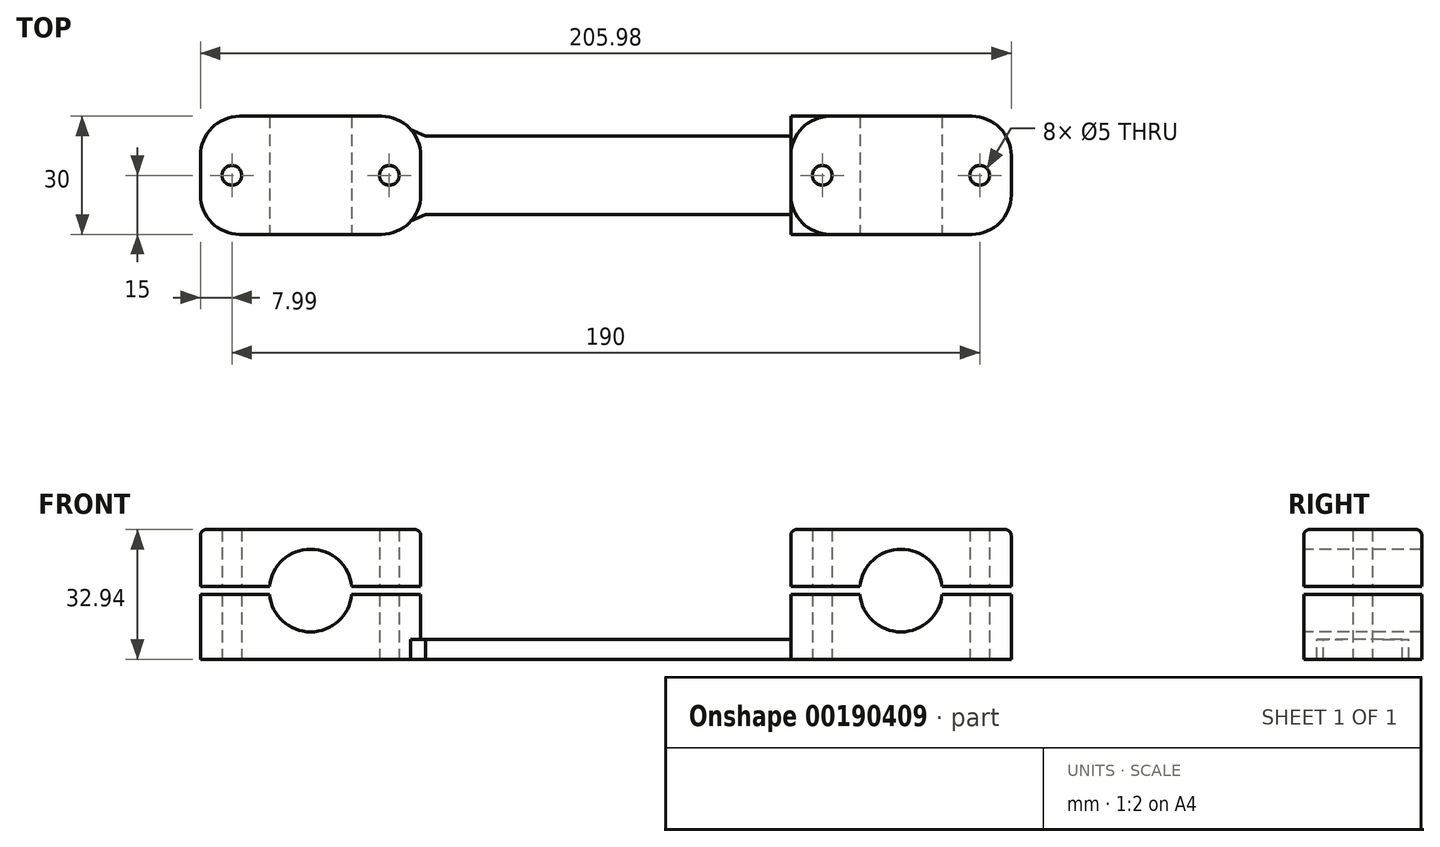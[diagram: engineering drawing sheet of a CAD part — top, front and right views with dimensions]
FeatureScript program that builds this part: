
annotation { "Feature Type Name" : "Feature", "Feature Type Description" : "" }
export const myFeature = defineFeature(function(context is Context, id is Id, definition is map)
    precondition{}
    {
        {
            var Q0;
            Q0=qCreatedBy(makeId("Top.planeOp"),FACE);
            var sketch = newSketch(context, id + "F0", { "sketchPlane" : qUnion([Q0])});
            skLineSegment(sketch, "E0.bottom", {"start": v(103, 15) * mm, "end": v(-103, 15) * mm});
            skLineSegment(sketch, "E0.top", {"start": v(103, -15) * mm, "end": v(-103, -15) * mm});
            skLineSegment(sketch, "E0.left", {"start": v(103, 15) * mm, "end": v(103, -15) * mm});
            skLineSegment(sketch, "E0.right", {"start": v(-103, 15) * mm, "end": v(-103, -15) * mm});
            skPoint(sketch, "E0.middle", {"position": v(0, 0) * mm});
            skLineSegment(sketch, "E1", {"start": v(75, 6.2) * mm, "end": v(75, -7.56) * mm, "construction": true});
            skCircle(sketch, "E2", {"center": v(95, 0) * mm, "radius": 2.5 * mm});
            skCircle(sketch, "E3.MirrorC", {"center": v(55, 0) * mm, "radius": 2.5 * mm});
            skCircle(sketch, "E4.MirrorC", {"center": v(-55, 0) * mm, "radius": 2.5 * mm});
            skCircle(sketch, "E5.MirrorC", {"center": v(-95, 0) * mm, "radius": 2.5 * mm});
            skLineSegment(sketch, "E6.MirrorCS", {"start": v(-75, 6.2) * mm, "end": v(-75, -7.56) * mm, "construction": true});
            skSolve(sketch);
        }
        {
            var Q0;
            Q0 = qSketchRegion(id + "F0", true);
            extrude(context, id + "F1", {"entities" : qUnion([Q0]), "depth" : 5 * mm});
        }
        {
            var Q0;
            Q0=makeQuery(id+"F1.opExtrude","SWEPT_FACE",FACE,{"disambiguationData":[OSD([sQuery(id+"F0.wireOp",EDGE,"E0.top")])]});
            var sketch = newSketch(context, id + "F2", { "sketchPlane" : qUnion([Q0])});
            skCircle(sketch, "E7", {"center": v(-75, 17.44) * mm, "radius": 10.5 * mm});
            skLineSegment(sketch, "E8.bottom", {"start": v(-103, 5) * mm, "end": v(-47, 5) * mm});
            skLineSegment(sketch, "E8.top", {"start": v(-103, 32.94) * mm, "end": v(-47, 32.94) * mm});
            skLineSegment(sketch, "E8.left", {"start": v(-103, 5) * mm, "end": v(-103, 32.94) * mm});
            skLineSegment(sketch, "E8.right", {"start": v(-47, 5) * mm, "end": v(-47, 32.94) * mm});
            skLineSegment(sketch, "E9", {"start": v(-75, 17.44) * mm, "end": v(-75, 36.32) * mm, "construction": true});
            skLineSegment(sketch, "E10.MirrorCS", {"start": v(75, 17.44) * mm, "end": v(75, 36.32) * mm, "construction": true});
            skLineSegment(sketch, "E11.MirrorCS", {"start": v(47, 5) * mm, "end": v(47, 32.94) * mm});
            skLineSegment(sketch, "E12.MirrorCS", {"start": v(103, 5) * mm, "end": v(103, 32.94) * mm});
            skLineSegment(sketch, "E13.MirrorCS", {"start": v(103, 32.94) * mm, "end": v(47, 32.94) * mm});
            skCircle(sketch, "E14.MirrorC", {"center": v(75, 17.44) * mm, "radius": 10.5 * mm});
            skLineSegment(sketch, "E15.MirrorCS", {"start": v(103, 5) * mm, "end": v(47, 5) * mm});
            skSolve(sketch);
        }
        {
            var Q0;
            Q0 = qSketchRegion(id + "F2", true);
            var Q1;
            Q1=makeQuery(id+"F1.opExtrude","SWEPT_FACE",FACE,{"disambiguationData":[OSD([sQuery(id+"F0.wireOp",EDGE,"E0.bottom")])]});
            extrude(context, id + "F3", {"entities" : qUnion([Q0]), "operationType" : NewBodyOperationType.ADD, "endBound" : BoundingType.UP_TO_SURFACE, "oppositeDirection" : true, "endBoundEntityFace" : qUnion([Q1]), "depth" : 25 * mm});
        }
        {
            var Q0;
            Q0=makeQuery(id+"F3.boolean.opBoolean","SPLIT",FACE,{"disambiguationData":[TD([makeQuery(id+"F1.opExtrude","SWEPT_FACE",FACE,{"disambiguationData":[OSD([sQuery(id+"F0.wireOp",EDGE,"E5.MirrorC")])]})])],"derivedFrom":makeQuery(id+"F3.opExtrude","SWEPT_FACE",FACE,{"disambiguationData":[OSD([sQuery(id+"F2.wireOp",EDGE,"E8.bottom")])]})});
            var Q1;
            Q1=makeQuery(id+"F3.boolean.opBoolean","SPLIT",FACE,{"disambiguationData":[TD([makeQuery(id+"F1.opExtrude","SWEPT_FACE",FACE,{"disambiguationData":[OSD([sQuery(id+"F0.wireOp",EDGE,"E4.MirrorC")])]})])],"derivedFrom":makeQuery(id+"F3.opExtrude","SWEPT_FACE",FACE,{"disambiguationData":[OSD([sQuery(id+"F2.wireOp",EDGE,"E8.bottom")])]})});
            var Q2;
            Q2=makeQuery(id+"F3.boolean.opBoolean","SPLIT",FACE,{"disambiguationData":[TD([makeQuery(id+"F1.opExtrude","SWEPT_FACE",FACE,{"disambiguationData":[OSD([sQuery(id+"F0.wireOp",EDGE,"E3.MirrorC")])]})])],"derivedFrom":makeQuery(id+"F3.opExtrude","SWEPT_FACE",FACE,{"disambiguationData":[OSD([sQuery(id+"F2.wireOp",EDGE,"E15.MirrorCS")])]})});
            var Q3;
            Q3=makeQuery(id+"F3.boolean.opBoolean","SPLIT",FACE,{"disambiguationData":[TD([makeQuery(id+"F1.opExtrude","SWEPT_FACE",FACE,{"disambiguationData":[OSD([sQuery(id+"F0.wireOp",EDGE,"E2")])]})])],"derivedFrom":makeQuery(id+"F3.opExtrude","SWEPT_FACE",FACE,{"disambiguationData":[OSD([sQuery(id+"F2.wireOp",EDGE,"E15.MirrorCS")])]})});
            var Q4;
            Q4=makeQuery(id+"F3.opExtrude","SWEPT_FACE",FACE,{"disambiguationData":[OSD([sQuery(id+"F2.wireOp",EDGE,"E8.top")])]});
            extrude(context, id + "F4", {"entities" : qUnion([Q0, Q1, Q2, Q3]), "operationType" : NewBodyOperationType.REMOVE, "endBound" : BoundingType.UP_TO_SURFACE, "oppositeDirection" : true, "endBoundEntityFace" : qUnion([Q4]), "depth" : 25 * mm});
        }
        {
            var Q0;
            Q0=makeQuery(id+"F3.boolean.opBoolean","MERGE",FACE,{"derivedFrom":[makeQuery(id+"F1.opExtrude","SWEPT_FACE",FACE,{"disambiguationData":[OSD([sQuery(id+"F0.wireOp",EDGE,"E0.bottom")])]}),makeQuery(id+"F3.opExtrude","CAP_FACE",FACE,{"disambiguationData":[OSD([sQuery(id+"F2.wireOp",EDGE,"E7"),sQuery(id+"F2.wireOp",EDGE,"E8.bottom"),sQuery(id+"F2.wireOp",EDGE,"E8.top"),sQuery(id+"F2.wireOp",EDGE,"E8.left"),sQuery(id+"F2.wireOp",EDGE,"E8.right")])],"isStart":false}),makeQuery(id+"F3.opExtrude","CAP_FACE",FACE,{"disambiguationData":[OSD([sQuery(id+"F2.wireOp",EDGE,"E11.MirrorCS"),sQuery(id+"F2.wireOp",EDGE,"E12.MirrorCS"),sQuery(id+"F2.wireOp",EDGE,"E13.MirrorCS"),sQuery(id+"F2.wireOp",EDGE,"E14.MirrorC"),sQuery(id+"F2.wireOp",EDGE,"E15.MirrorCS")])],"isStart":false})]});
            var sketch = newSketch(context, id + "F5", { "sketchPlane" : qUnion([Q0])});
            skLineSegment(sketch, "E16.bottom", {"start": v(-103, 16.47) * mm, "end": v(103, 16.47) * mm});
            skLineSegment(sketch, "E16.top", {"start": v(-103, 18.47) * mm, "end": v(103, 18.47) * mm});
            skLineSegment(sketch, "E16.left", {"start": v(-103, 16.47) * mm, "end": v(-103, 18.47) * mm});
            skLineSegment(sketch, "E16.right", {"start": v(103, 16.47) * mm, "end": v(103, 18.47) * mm});
            skSolve(sketch);
        }
        {
            var Q0;
            Q0 = qSketchRegion(id + "F5", true);
            extrude(context, id + "F6", {"entities" : qUnion([Q0]), "operationType" : NewBodyOperationType.REMOVE, "endBound" : BoundingType.THROUGH_ALL, "oppositeDirection" : true, "depth" : 25 * mm});
        }
        {
            var Q0;
            Q0=makeQuery(id+"F1.opExtrude","CAP_FACE",FACE,{"disambiguationData":[OSD([sQuery(id+"F0.wireOp",EDGE,"E0.bottom"),sQuery(id+"F0.wireOp",EDGE,"E0.top"),sQuery(id+"F0.wireOp",EDGE,"E0.left"),sQuery(id+"F0.wireOp",EDGE,"E0.right"),sQuery(id+"F0.wireOp",EDGE,"E2"),sQuery(id+"F0.wireOp",EDGE,"E3.MirrorC"),sQuery(id+"F0.wireOp",EDGE,"E4.MirrorC"),sQuery(id+"F0.wireOp",EDGE,"E5.MirrorC")])],"isStart":false});
            var sketch = newSketch(context, id + "F7", { "sketchPlane" : qUnion([Q0])});
            skLineSegment(sketch, "E17.bottom", {"start": v(-47, 15) * mm, "end": v(47, 15) * mm});
            skLineSegment(sketch, "E17.top", {"start": v(-47, 10) * mm, "end": v(47, 10) * mm});
            skLineSegment(sketch, "E17.left", {"start": v(-47, 15) * mm, "end": v(-47, 10) * mm});
            skLineSegment(sketch, "E17.right", {"start": v(47, 15) * mm, "end": v(47, 10) * mm});
            skLineSegment(sketch, "E18.MirrorCS", {"start": v(47, -15) * mm, "end": v(47, -10) * mm});
            skLineSegment(sketch, "E19.MirrorCS", {"start": v(-47, -15) * mm, "end": v(-47, -10) * mm});
            skLineSegment(sketch, "E20.MirrorCS", {"start": v(-47, -10) * mm, "end": v(47, -10) * mm});
            skLineSegment(sketch, "E21.MirrorCS", {"start": v(-47, -15) * mm, "end": v(47, -15) * mm});
            skSolve(sketch);
        }
        {
            var Q0;
            Q0 = qSketchRegion(id + "F7", true);
            extrude(context, id + "F8", {"entities" : qUnion([Q0]), "operationType" : NewBodyOperationType.REMOVE, "endBound" : BoundingType.THROUGH_ALL, "oppositeDirection" : true, "depth" : 25 * mm});
        }
        {
            var Q0;
            {var subQ0=sQuery(id+"F2.wireOp",EDGE,"E8.top");var subQ1=sQuery(id+"F0.wireOp",EDGE,"E0.right");var subQ2=sQuery(id+"F2.wireOp",EDGE,"E8.left");var subQ3=sQuery(id+"F0.wireOp",EDGE,"E0.top");Q0=makeQuery(id+"F6.boolean.opBoolean","SPLIT",EDGE,{"disambiguationData":[TD([makeQuery(id+"F3.opExtrude","SWEPT_FACE",FACE,{"disambiguationData":[OSD([subQ0])]})])],"derivedFrom":makeQuery(id+"F3.boolean.opBoolean","MERGE",EDGE,{"derivedFrom":[makeQuery(id+"F1.opExtrude","SWEPT_EDGE",EDGE,{"disambiguationData":[OSD([subQ3,subQ1])]}),makeQuery(id+"F3.opExtrude","CAP_EDGE",EDGE,{"disambiguationData":[OSD([subQ2])],"isStart":true})]})});}
            var Q1;
            {var subQ0=sQuery(id+"F2.wireOp",EDGE,"E8.left");var subQ1=sQuery(id+"F0.wireOp",EDGE,"E0.right");var subQ2=sQuery(id+"F0.wireOp",EDGE,"E0.top");Q1=makeQuery(id+"F6.boolean.opBoolean","SPLIT",EDGE,{"disambiguationData":[TD([makeQuery(id+"F6.opExtrude","SWEPT_FACE",FACE,{"disambiguationData":[OSD([sQuery(id+"F5.wireOp",EDGE,"E16.bottom")])]})])],"derivedFrom":makeQuery(id+"F3.boolean.opBoolean","MERGE",EDGE,{"derivedFrom":[makeQuery(id+"F1.opExtrude","SWEPT_EDGE",EDGE,{"disambiguationData":[OSD([subQ2,subQ1])]}),makeQuery(id+"F3.opExtrude","CAP_EDGE",EDGE,{"disambiguationData":[OSD([subQ0])],"isStart":true})]})});}
            var Q2;
            {var subQ0=sQuery(id+"F2.wireOp",EDGE,"E8.top");var subQ1=sQuery(id+"F0.wireOp",EDGE,"E0.right");var subQ2=sQuery(id+"F2.wireOp",EDGE,"E8.left");var subQ3=sQuery(id+"F0.wireOp",EDGE,"E0.bottom");Q2=makeQuery(id+"F6.boolean.opBoolean","SPLIT",EDGE,{"disambiguationData":[TD([makeQuery(id+"F3.opExtrude","SWEPT_FACE",FACE,{"disambiguationData":[OSD([subQ0])]})])],"derivedFrom":makeQuery(id+"F3.boolean.opBoolean","MERGE",EDGE,{"derivedFrom":[makeQuery(id+"F1.opExtrude","SWEPT_EDGE",EDGE,{"disambiguationData":[OSD([subQ3,subQ1])]}),makeQuery(id+"F3.opExtrude","CAP_EDGE",EDGE,{"disambiguationData":[OSD([subQ2])],"isStart":false})]})});}
            var Q3;
            {var subQ0=sQuery(id+"F0.wireOp",EDGE,"E0.right");var subQ1=sQuery(id+"F0.wireOp",EDGE,"E0.bottom");var subQ2=sQuery(id+"F2.wireOp",EDGE,"E8.left");Q3=makeQuery(id+"F6.boolean.opBoolean","SPLIT",EDGE,{"disambiguationData":[TD([makeQuery(id+"F6.opExtrude","SWEPT_FACE",FACE,{"disambiguationData":[OSD([sQuery(id+"F5.wireOp",EDGE,"E16.bottom")])]})])],"derivedFrom":makeQuery(id+"F3.boolean.opBoolean","MERGE",EDGE,{"derivedFrom":[makeQuery(id+"F1.opExtrude","SWEPT_EDGE",EDGE,{"disambiguationData":[OSD([subQ1,subQ0])]}),makeQuery(id+"F3.opExtrude","CAP_EDGE",EDGE,{"disambiguationData":[OSD([subQ2])],"isStart":false})]})});}
            var Q4;
            {var subQ0=sQuery(id+"F2.wireOp",EDGE,"E8.right");Q4=makeQuery(id+"F8.boolean.opBoolean","MERGE",EDGE,{"derivedFrom":[makeQuery(id+"F6.boolean.opBoolean","SPLIT",EDGE,{"disambiguationData":[TD([makeQuery(id+"F6.opExtrude","SWEPT_FACE",FACE,{"disambiguationData":[OSD([sQuery(id+"F5.wireOp",EDGE,"E16.bottom")])]})])],"derivedFrom":makeQuery(id+"F3.opExtrude","CAP_EDGE",EDGE,{"disambiguationData":[OSD([subQ0])],"isStart":true})})],"fromTools":[makeQuery(id+"F8.opExtrude","SWEPT_EDGE",EDGE,{"disambiguationData":[OSD([sQuery(id+"F7.wireOp",EDGE,"E19.MirrorCS"),sQuery(id+"F7.wireOp",EDGE,"E21.MirrorCS")])]})]});}
            var Q5;
            {var subQ0=sQuery(id+"F2.wireOp",EDGE,"E8.right");var subQ1=sQuery(id+"F2.wireOp",EDGE,"E8.top");Q5=makeQuery(id+"F6.boolean.opBoolean","SPLIT",EDGE,{"disambiguationData":[TD([makeQuery(id+"F3.opExtrude","SWEPT_FACE",FACE,{"disambiguationData":[OSD([subQ1])]})])],"derivedFrom":makeQuery(id+"F3.opExtrude","CAP_EDGE",EDGE,{"disambiguationData":[OSD([subQ0])],"isStart":false})});}
            var Q6;
            {var subQ0=sQuery(id+"F2.wireOp",EDGE,"E8.right");Q6=makeQuery(id+"F8.boolean.opBoolean","MERGE",EDGE,{"derivedFrom":[makeQuery(id+"F6.boolean.opBoolean","SPLIT",EDGE,{"disambiguationData":[TD([makeQuery(id+"F6.opExtrude","SWEPT_FACE",FACE,{"disambiguationData":[OSD([sQuery(id+"F5.wireOp",EDGE,"E16.bottom")])]})])],"derivedFrom":makeQuery(id+"F3.opExtrude","CAP_EDGE",EDGE,{"disambiguationData":[OSD([subQ0])],"isStart":false})})],"fromTools":[makeQuery(id+"F8.opExtrude","SWEPT_EDGE",EDGE,{"disambiguationData":[OSD([sQuery(id+"F7.wireOp",EDGE,"E17.bottom"),sQuery(id+"F7.wireOp",EDGE,"E17.left")])]})]});}
            var Q7;
            {var subQ1=sQuery(id+"F2.wireOp",EDGE,"E11.MirrorCS");Q7=makeQuery(id+"F8.boolean.opBoolean","MERGE",EDGE,{"derivedFrom":[makeQuery(id+"F6.boolean.opBoolean","SPLIT",EDGE,{"disambiguationData":[TD([makeQuery(id+"F6.opExtrude","SWEPT_FACE",FACE,{"disambiguationData":[OSD([sQuery(id+"F5.wireOp",EDGE,"E16.bottom")])]})])],"derivedFrom":makeQuery(id+"F3.opExtrude","CAP_EDGE",EDGE,{"disambiguationData":[OSD([subQ1])],"isStart":false})})],"fromTools":[makeQuery(id+"F8.opExtrude","SWEPT_EDGE",EDGE,{"disambiguationData":[OSD([sQuery(id+"F7.wireOp",EDGE,"E17.bottom"),sQuery(id+"F7.wireOp",EDGE,"E17.right")])]})]});}
            var Q8;
            {var subQ0=sQuery(id+"F2.wireOp",EDGE,"E13.MirrorCS");var subQ1=sQuery(id+"F2.wireOp",EDGE,"E11.MirrorCS");Q8=makeQuery(id+"F6.boolean.opBoolean","SPLIT",EDGE,{"disambiguationData":[TD([makeQuery(id+"F3.opExtrude","SWEPT_FACE",FACE,{"disambiguationData":[OSD([subQ0])]})])],"derivedFrom":makeQuery(id+"F3.opExtrude","CAP_EDGE",EDGE,{"disambiguationData":[OSD([subQ1])],"isStart":false})});}
            var Q9;
            {var subQ0=sQuery(id+"F2.wireOp",EDGE,"E13.MirrorCS");var subQ1=sQuery(id+"F2.wireOp",EDGE,"E11.MirrorCS");Q9=makeQuery(id+"F6.boolean.opBoolean","SPLIT",EDGE,{"disambiguationData":[TD([makeQuery(id+"F3.opExtrude","SWEPT_FACE",FACE,{"disambiguationData":[OSD([subQ0])]})])],"derivedFrom":makeQuery(id+"F3.opExtrude","CAP_EDGE",EDGE,{"disambiguationData":[OSD([subQ1])],"isStart":true})});}
            var Q10;
            {var subQ0=sQuery(id+"F2.wireOp",EDGE,"E11.MirrorCS");Q10=makeQuery(id+"F8.boolean.opBoolean","MERGE",EDGE,{"derivedFrom":[makeQuery(id+"F6.boolean.opBoolean","SPLIT",EDGE,{"disambiguationData":[TD([makeQuery(id+"F6.opExtrude","SWEPT_FACE",FACE,{"disambiguationData":[OSD([sQuery(id+"F5.wireOp",EDGE,"E16.bottom")])]})])],"derivedFrom":makeQuery(id+"F3.opExtrude","CAP_EDGE",EDGE,{"disambiguationData":[OSD([subQ0])],"isStart":true})})],"fromTools":[makeQuery(id+"F8.opExtrude","SWEPT_EDGE",EDGE,{"disambiguationData":[OSD([sQuery(id+"F7.wireOp",EDGE,"E18.MirrorCS"),sQuery(id+"F7.wireOp",EDGE,"E21.MirrorCS")])]})]});}
            var Q11;
            {var subQ0=sQuery(id+"F2.wireOp",EDGE,"E13.MirrorCS");var subQ1=sQuery(id+"F2.wireOp",EDGE,"E12.MirrorCS");var subQ2=sQuery(id+"F0.wireOp",EDGE,"E0.left");var subQ3=sQuery(id+"F0.wireOp",EDGE,"E0.top");Q11=makeQuery(id+"F6.boolean.opBoolean","SPLIT",EDGE,{"disambiguationData":[TD([makeQuery(id+"F3.opExtrude","SWEPT_FACE",FACE,{"disambiguationData":[OSD([subQ0])]})])],"derivedFrom":makeQuery(id+"F3.boolean.opBoolean","MERGE",EDGE,{"derivedFrom":[makeQuery(id+"F1.opExtrude","SWEPT_EDGE",EDGE,{"disambiguationData":[OSD([subQ3,subQ2])]}),makeQuery(id+"F3.opExtrude","CAP_EDGE",EDGE,{"disambiguationData":[OSD([subQ1])],"isStart":true})]})});}
            var Q12;
            {var subQ0=sQuery(id+"F0.wireOp",EDGE,"E0.left");var subQ1=sQuery(id+"F0.wireOp",EDGE,"E0.top");var subQ2=sQuery(id+"F2.wireOp",EDGE,"E12.MirrorCS");Q12=makeQuery(id+"F6.boolean.opBoolean","SPLIT",EDGE,{"disambiguationData":[TD([makeQuery(id+"F6.opExtrude","SWEPT_FACE",FACE,{"disambiguationData":[OSD([sQuery(id+"F5.wireOp",EDGE,"E16.bottom")])]})])],"derivedFrom":makeQuery(id+"F3.boolean.opBoolean","MERGE",EDGE,{"derivedFrom":[makeQuery(id+"F1.opExtrude","SWEPT_EDGE",EDGE,{"disambiguationData":[OSD([subQ1,subQ0])]}),makeQuery(id+"F3.opExtrude","CAP_EDGE",EDGE,{"disambiguationData":[OSD([subQ2])],"isStart":true})]})});}
            var Q13;
            {var subQ0=sQuery(id+"F0.wireOp",EDGE,"E0.left");var subQ1=sQuery(id+"F0.wireOp",EDGE,"E0.bottom");var subQ2=sQuery(id+"F2.wireOp",EDGE,"E12.MirrorCS");Q13=makeQuery(id+"F6.boolean.opBoolean","SPLIT",EDGE,{"disambiguationData":[TD([makeQuery(id+"F6.opExtrude","SWEPT_FACE",FACE,{"disambiguationData":[OSD([sQuery(id+"F5.wireOp",EDGE,"E16.bottom")])]})])],"derivedFrom":makeQuery(id+"F3.boolean.opBoolean","MERGE",EDGE,{"derivedFrom":[makeQuery(id+"F1.opExtrude","SWEPT_EDGE",EDGE,{"disambiguationData":[OSD([subQ1,subQ0])]}),makeQuery(id+"F3.opExtrude","CAP_EDGE",EDGE,{"disambiguationData":[OSD([subQ2])],"isStart":false})]})});}
            var Q14;
            {var subQ0=sQuery(id+"F2.wireOp",EDGE,"E13.MirrorCS");var subQ1=sQuery(id+"F2.wireOp",EDGE,"E12.MirrorCS");var subQ2=sQuery(id+"F0.wireOp",EDGE,"E0.left");var subQ3=sQuery(id+"F0.wireOp",EDGE,"E0.bottom");Q14=makeQuery(id+"F6.boolean.opBoolean","SPLIT",EDGE,{"disambiguationData":[TD([makeQuery(id+"F3.opExtrude","SWEPT_FACE",FACE,{"disambiguationData":[OSD([subQ0])]})])],"derivedFrom":makeQuery(id+"F3.boolean.opBoolean","MERGE",EDGE,{"derivedFrom":[makeQuery(id+"F1.opExtrude","SWEPT_EDGE",EDGE,{"disambiguationData":[OSD([subQ3,subQ2])]}),makeQuery(id+"F3.opExtrude","CAP_EDGE",EDGE,{"disambiguationData":[OSD([subQ1])],"isStart":false})]})});}
            var Q15;
            {var subQ0=sQuery(id+"F2.wireOp",EDGE,"E8.top");var subQ1=sQuery(id+"F2.wireOp",EDGE,"E8.right");Q15=makeQuery(id+"F6.boolean.opBoolean","SPLIT",EDGE,{"disambiguationData":[TD([makeQuery(id+"F3.opExtrude","SWEPT_FACE",FACE,{"disambiguationData":[OSD([subQ0])]})])],"derivedFrom":makeQuery(id+"F3.opExtrude","CAP_EDGE",EDGE,{"disambiguationData":[OSD([subQ1])],"isStart":true})});}
            fillet(context, id + "F9", {"entities" : qUnion([Q0, Q1, Q2, Q3, Q4, Q5, Q6, Q7, Q8, Q9, Q10, Q11, Q12, Q13, Q14, Q15]), "radius" : 10 * mm, "tangentPropagation" : true, "allowEdgeOverflow" : false});
        }
        {
            var Q0;
            {var subQ0=sQuery(id+"F2.wireOp",EDGE,"E8.right");Q0=makeQuery(id+"F9.opFillet","BLEND_EDGE",EDGE,{"blendedFrom":[makeQuery(id+"F8.boolean.opBoolean","MERGE",EDGE,{"derivedFrom":[makeQuery(id+"F6.boolean.opBoolean","SPLIT",EDGE,{"disambiguationData":[TD([makeQuery(id+"F6.opExtrude","SWEPT_FACE",FACE,{"disambiguationData":[OSD([sQuery(id+"F5.wireOp",EDGE,"E16.bottom")])]})])],"derivedFrom":makeQuery(id+"F3.opExtrude","CAP_EDGE",EDGE,{"disambiguationData":[OSD([subQ0])],"isStart":true})})],"fromTools":[makeQuery(id+"F8.opExtrude","SWEPT_EDGE",EDGE,{"disambiguationData":[OSD([sQuery(id+"F7.wireOp",EDGE,"E19.MirrorCS"),sQuery(id+"F7.wireOp",EDGE,"E21.MirrorCS")])]})]}),makeQuery(id+"F8.boolean.opBoolean","COPY",FACE,{"derivedFrom":makeQuery(id+"F8.opExtrude","SWEPT_FACE",FACE,{"disambiguationData":[OSD([sQuery(id+"F7.wireOp",EDGE,"E20.MirrorCS")])]})})],"blendedInto":[makeQuery(id+"F8.boolean.opBoolean","COPY",FACE,{"derivedFrom":makeQuery(id+"F8.opExtrude","SWEPT_FACE",FACE,{"disambiguationData":[OSD([sQuery(id+"F7.wireOp",EDGE,"E20.MirrorCS")])]})})]});}
            var Q1;
            {var subQ0=sQuery(id+"F2.wireOp",EDGE,"E11.MirrorCS");Q1=makeQuery(id+"F9.opFillet","BLEND_EDGE",EDGE,{"blendedFrom":[makeQuery(id+"F8.boolean.opBoolean","MERGE",EDGE,{"derivedFrom":[makeQuery(id+"F6.boolean.opBoolean","SPLIT",EDGE,{"disambiguationData":[TD([makeQuery(id+"F6.opExtrude","SWEPT_FACE",FACE,{"disambiguationData":[OSD([sQuery(id+"F5.wireOp",EDGE,"E16.bottom")])]})])],"derivedFrom":makeQuery(id+"F3.opExtrude","CAP_EDGE",EDGE,{"disambiguationData":[OSD([subQ0])],"isStart":true})})],"fromTools":[makeQuery(id+"F8.opExtrude","SWEPT_EDGE",EDGE,{"disambiguationData":[OSD([sQuery(id+"F7.wireOp",EDGE,"E18.MirrorCS"),sQuery(id+"F7.wireOp",EDGE,"E21.MirrorCS")])]})]}),makeQuery(id+"F8.boolean.opBoolean","COPY",FACE,{"derivedFrom":makeQuery(id+"F8.opExtrude","SWEPT_FACE",FACE,{"disambiguationData":[OSD([sQuery(id+"F7.wireOp",EDGE,"E20.MirrorCS")])]})})],"blendedInto":[makeQuery(id+"F8.boolean.opBoolean","COPY",FACE,{"derivedFrom":makeQuery(id+"F8.opExtrude","SWEPT_FACE",FACE,{"disambiguationData":[OSD([sQuery(id+"F7.wireOp",EDGE,"E20.MirrorCS")])]})})]});}
            var Q2;
            {var subQ0=sQuery(id+"F2.wireOp",EDGE,"E8.right");Q2=makeQuery(id+"F9.opFillet","BLEND_EDGE",EDGE,{"blendedFrom":[makeQuery(id+"F8.boolean.opBoolean","MERGE",EDGE,{"derivedFrom":[makeQuery(id+"F6.boolean.opBoolean","SPLIT",EDGE,{"disambiguationData":[TD([makeQuery(id+"F6.opExtrude","SWEPT_FACE",FACE,{"disambiguationData":[OSD([sQuery(id+"F5.wireOp",EDGE,"E16.bottom")])]})])],"derivedFrom":makeQuery(id+"F3.opExtrude","CAP_EDGE",EDGE,{"disambiguationData":[OSD([subQ0])],"isStart":false})})],"fromTools":[makeQuery(id+"F8.opExtrude","SWEPT_EDGE",EDGE,{"disambiguationData":[OSD([sQuery(id+"F7.wireOp",EDGE,"E17.bottom"),sQuery(id+"F7.wireOp",EDGE,"E17.left")])]})]}),makeQuery(id+"F8.boolean.opBoolean","COPY",FACE,{"derivedFrom":makeQuery(id+"F8.opExtrude","SWEPT_FACE",FACE,{"disambiguationData":[OSD([sQuery(id+"F7.wireOp",EDGE,"E17.top")])]})})],"blendedInto":[makeQuery(id+"F8.boolean.opBoolean","COPY",FACE,{"derivedFrom":makeQuery(id+"F8.opExtrude","SWEPT_FACE",FACE,{"disambiguationData":[OSD([sQuery(id+"F7.wireOp",EDGE,"E17.top")])]})})]});}
            var Q3;
            {var subQ1=sQuery(id+"F2.wireOp",EDGE,"E11.MirrorCS");Q3=makeQuery(id+"F9.opFillet","BLEND_EDGE",EDGE,{"blendedFrom":[makeQuery(id+"F8.boolean.opBoolean","MERGE",EDGE,{"derivedFrom":[makeQuery(id+"F6.boolean.opBoolean","SPLIT",EDGE,{"disambiguationData":[TD([makeQuery(id+"F6.opExtrude","SWEPT_FACE",FACE,{"disambiguationData":[OSD([sQuery(id+"F5.wireOp",EDGE,"E16.bottom")])]})])],"derivedFrom":makeQuery(id+"F3.opExtrude","CAP_EDGE",EDGE,{"disambiguationData":[OSD([subQ1])],"isStart":false})})],"fromTools":[makeQuery(id+"F8.opExtrude","SWEPT_EDGE",EDGE,{"disambiguationData":[OSD([sQuery(id+"F7.wireOp",EDGE,"E17.bottom"),sQuery(id+"F7.wireOp",EDGE,"E17.right")])]})]}),makeQuery(id+"F8.boolean.opBoolean","COPY",FACE,{"derivedFrom":makeQuery(id+"F8.opExtrude","SWEPT_FACE",FACE,{"disambiguationData":[OSD([sQuery(id+"F7.wireOp",EDGE,"E17.top")])]})})],"blendedInto":[makeQuery(id+"F8.boolean.opBoolean","COPY",FACE,{"derivedFrom":makeQuery(id+"F8.opExtrude","SWEPT_FACE",FACE,{"disambiguationData":[OSD([sQuery(id+"F7.wireOp",EDGE,"E17.top")])]})})]});}
            chamfer(context, id + "F10", {"entities" : qUnion([Q0, Q1, Q2, Q3]), "width" : 5 * mm, "tangentPropagation" : true});
        }
        {
            var Q0;
            Q0=makeQuery(id+"F8.boolean.opBoolean","COPY",EDGE,{"derivedFrom":makeQuery(id+"F8.opExtrude","CAP_EDGE",EDGE,{"disambiguationData":[OSD([sQuery(id+"F7.wireOp",EDGE,"E20.MirrorCS")])],"isStart":true})});
            var Q1;
            Q1=makeQuery(id+"F8.boolean.opBoolean","COPY",EDGE,{"derivedFrom":makeQuery(id+"F8.opExtrude","CAP_EDGE",EDGE,{"disambiguationData":[OSD([sQuery(id+"F7.wireOp",EDGE,"E17.top")])],"isStart":true})});
            var Q2;
            {var subQ0=sQuery(id+"F0.wireOp",EDGE,"E0.top");var subQ1=makeQuery(id+"F1.opExtrude","CAP_FACE",FACE,{"disambiguationData":[OSD([sQuery(id+"F0.wireOp",EDGE,"E0.bottom"),subQ0,sQuery(id+"F0.wireOp",EDGE,"E0.left"),sQuery(id+"F0.wireOp",EDGE,"E0.right"),sQuery(id+"F0.wireOp",EDGE,"E2"),sQuery(id+"F0.wireOp",EDGE,"E3.MirrorC"),sQuery(id+"F0.wireOp",EDGE,"E4.MirrorC"),sQuery(id+"F0.wireOp",EDGE,"E5.MirrorC")])],"isStart":false});var subQ2=sQuery(id+"F2.wireOp",EDGE,"E11.MirrorCS");Q2=makeQuery(id+"F10.opChamfer","BLEND_EDGE",EDGE,{"blendedFrom":[makeQuery(id+"F9.opFillet","BLEND_EDGE",EDGE,{"blendedFrom":[makeQuery(id+"F8.boolean.opBoolean","MERGE",EDGE,{"derivedFrom":[makeQuery(id+"F6.boolean.opBoolean","SPLIT",EDGE,{"disambiguationData":[TD([makeQuery(id+"F6.opExtrude","SWEPT_FACE",FACE,{"disambiguationData":[OSD([sQuery(id+"F5.wireOp",EDGE,"E16.bottom")])]})])],"derivedFrom":makeQuery(id+"F3.opExtrude","CAP_EDGE",EDGE,{"disambiguationData":[OSD([subQ2])],"isStart":true})})],"fromTools":[makeQuery(id+"F8.opExtrude","SWEPT_EDGE",EDGE,{"disambiguationData":[OSD([sQuery(id+"F7.wireOp",EDGE,"E18.MirrorCS"),sQuery(id+"F7.wireOp",EDGE,"E21.MirrorCS")])]})]}),makeQuery(id+"F8.boolean.opBoolean","COPY",FACE,{"derivedFrom":makeQuery(id+"F8.opExtrude","SWEPT_FACE",FACE,{"disambiguationData":[OSD([sQuery(id+"F7.wireOp",EDGE,"E20.MirrorCS")])]})})],"blendedInto":[makeQuery(id+"F8.boolean.opBoolean","COPY",FACE,{"derivedFrom":makeQuery(id+"F8.opExtrude","SWEPT_FACE",FACE,{"disambiguationData":[OSD([sQuery(id+"F7.wireOp",EDGE,"E20.MirrorCS")])]})})]}),subQ1],"blendedInto":[subQ1]});}
            var Q3;
            {var subQ0=sQuery(id+"F0.wireOp",EDGE,"E0.bottom");var subQ1=makeQuery(id+"F1.opExtrude","CAP_FACE",FACE,{"disambiguationData":[OSD([subQ0,sQuery(id+"F0.wireOp",EDGE,"E0.top"),sQuery(id+"F0.wireOp",EDGE,"E0.left"),sQuery(id+"F0.wireOp",EDGE,"E0.right"),sQuery(id+"F0.wireOp",EDGE,"E2"),sQuery(id+"F0.wireOp",EDGE,"E3.MirrorC"),sQuery(id+"F0.wireOp",EDGE,"E4.MirrorC"),sQuery(id+"F0.wireOp",EDGE,"E5.MirrorC")])],"isStart":false});var subQ2=sQuery(id+"F2.wireOp",EDGE,"E11.MirrorCS");Q3=makeQuery(id+"F10.opChamfer","BLEND_EDGE",EDGE,{"blendedFrom":[makeQuery(id+"F9.opFillet","BLEND_EDGE",EDGE,{"blendedFrom":[makeQuery(id+"F8.boolean.opBoolean","MERGE",EDGE,{"derivedFrom":[makeQuery(id+"F6.boolean.opBoolean","SPLIT",EDGE,{"disambiguationData":[TD([makeQuery(id+"F6.opExtrude","SWEPT_FACE",FACE,{"disambiguationData":[OSD([sQuery(id+"F5.wireOp",EDGE,"E16.bottom")])]})])],"derivedFrom":makeQuery(id+"F3.opExtrude","CAP_EDGE",EDGE,{"disambiguationData":[OSD([subQ2])],"isStart":false})})],"fromTools":[makeQuery(id+"F8.opExtrude","SWEPT_EDGE",EDGE,{"disambiguationData":[OSD([sQuery(id+"F7.wireOp",EDGE,"E17.bottom"),sQuery(id+"F7.wireOp",EDGE,"E17.right")])]})]}),makeQuery(id+"F8.boolean.opBoolean","COPY",FACE,{"derivedFrom":makeQuery(id+"F8.opExtrude","SWEPT_FACE",FACE,{"disambiguationData":[OSD([sQuery(id+"F7.wireOp",EDGE,"E17.top")])]})})],"blendedInto":[makeQuery(id+"F8.boolean.opBoolean","COPY",FACE,{"derivedFrom":makeQuery(id+"F8.opExtrude","SWEPT_FACE",FACE,{"disambiguationData":[OSD([sQuery(id+"F7.wireOp",EDGE,"E17.top")])]})})]}),subQ1],"blendedInto":[subQ1]});}
            var Q4;
            {var subQ0=sQuery(id+"F0.wireOp",EDGE,"E0.top");var subQ1=makeQuery(id+"F1.opExtrude","CAP_FACE",FACE,{"disambiguationData":[OSD([sQuery(id+"F0.wireOp",EDGE,"E0.bottom"),subQ0,sQuery(id+"F0.wireOp",EDGE,"E0.left"),sQuery(id+"F0.wireOp",EDGE,"E0.right"),sQuery(id+"F0.wireOp",EDGE,"E2"),sQuery(id+"F0.wireOp",EDGE,"E3.MirrorC"),sQuery(id+"F0.wireOp",EDGE,"E4.MirrorC"),sQuery(id+"F0.wireOp",EDGE,"E5.MirrorC")])],"isStart":false});var subQ2=sQuery(id+"F2.wireOp",EDGE,"E8.right");Q4=makeQuery(id+"F10.opChamfer","BLEND_EDGE",EDGE,{"blendedFrom":[makeQuery(id+"F9.opFillet","BLEND_EDGE",EDGE,{"blendedFrom":[makeQuery(id+"F8.boolean.opBoolean","MERGE",EDGE,{"derivedFrom":[makeQuery(id+"F6.boolean.opBoolean","SPLIT",EDGE,{"disambiguationData":[TD([makeQuery(id+"F6.opExtrude","SWEPT_FACE",FACE,{"disambiguationData":[OSD([sQuery(id+"F5.wireOp",EDGE,"E16.bottom")])]})])],"derivedFrom":makeQuery(id+"F3.opExtrude","CAP_EDGE",EDGE,{"disambiguationData":[OSD([subQ2])],"isStart":true})})],"fromTools":[makeQuery(id+"F8.opExtrude","SWEPT_EDGE",EDGE,{"disambiguationData":[OSD([sQuery(id+"F7.wireOp",EDGE,"E19.MirrorCS"),sQuery(id+"F7.wireOp",EDGE,"E21.MirrorCS")])]})]}),makeQuery(id+"F8.boolean.opBoolean","COPY",FACE,{"derivedFrom":makeQuery(id+"F8.opExtrude","SWEPT_FACE",FACE,{"disambiguationData":[OSD([sQuery(id+"F7.wireOp",EDGE,"E20.MirrorCS")])]})})],"blendedInto":[makeQuery(id+"F8.boolean.opBoolean","COPY",FACE,{"derivedFrom":makeQuery(id+"F8.opExtrude","SWEPT_FACE",FACE,{"disambiguationData":[OSD([sQuery(id+"F7.wireOp",EDGE,"E20.MirrorCS")])]})})]}),subQ1],"blendedInto":[subQ1]});}
            var Q5;
            {var subQ0=sQuery(id+"F0.wireOp",EDGE,"E0.bottom");var subQ1=makeQuery(id+"F1.opExtrude","CAP_FACE",FACE,{"disambiguationData":[OSD([subQ0,sQuery(id+"F0.wireOp",EDGE,"E0.top"),sQuery(id+"F0.wireOp",EDGE,"E0.left"),sQuery(id+"F0.wireOp",EDGE,"E0.right"),sQuery(id+"F0.wireOp",EDGE,"E2"),sQuery(id+"F0.wireOp",EDGE,"E3.MirrorC"),sQuery(id+"F0.wireOp",EDGE,"E4.MirrorC"),sQuery(id+"F0.wireOp",EDGE,"E5.MirrorC")])],"isStart":false});var subQ2=sQuery(id+"F2.wireOp",EDGE,"E8.right");Q5=makeQuery(id+"F10.opChamfer","BLEND_EDGE",EDGE,{"blendedFrom":[makeQuery(id+"F9.opFillet","BLEND_EDGE",EDGE,{"blendedFrom":[makeQuery(id+"F8.boolean.opBoolean","MERGE",EDGE,{"derivedFrom":[makeQuery(id+"F6.boolean.opBoolean","SPLIT",EDGE,{"disambiguationData":[TD([makeQuery(id+"F6.opExtrude","SWEPT_FACE",FACE,{"disambiguationData":[OSD([sQuery(id+"F5.wireOp",EDGE,"E16.bottom")])]})])],"derivedFrom":makeQuery(id+"F3.opExtrude","CAP_EDGE",EDGE,{"disambiguationData":[OSD([subQ2])],"isStart":false})})],"fromTools":[makeQuery(id+"F8.opExtrude","SWEPT_EDGE",EDGE,{"disambiguationData":[OSD([sQuery(id+"F7.wireOp",EDGE,"E17.bottom"),sQuery(id+"F7.wireOp",EDGE,"E17.left")])]})]}),makeQuery(id+"F8.boolean.opBoolean","COPY",FACE,{"derivedFrom":makeQuery(id+"F8.opExtrude","SWEPT_FACE",FACE,{"disambiguationData":[OSD([sQuery(id+"F7.wireOp",EDGE,"E17.top")])]})})],"blendedInto":[makeQuery(id+"F8.boolean.opBoolean","COPY",FACE,{"derivedFrom":makeQuery(id+"F8.opExtrude","SWEPT_FACE",FACE,{"disambiguationData":[OSD([sQuery(id+"F7.wireOp",EDGE,"E17.top")])]})})]}),subQ1],"blendedInto":[subQ1]});}
            var Q6;
            Q6=makeQuery(id+"F3.opExtrude","CAP_EDGE",EDGE,{"disambiguationData":[OSD([sQuery(id+"F2.wireOp",EDGE,"E8.top")])],"isStart":true});
            var Q7;
            Q7=makeQuery(id+"F3.opExtrude","CAP_EDGE",EDGE,{"disambiguationData":[OSD([sQuery(id+"F2.wireOp",EDGE,"E13.MirrorCS")])],"isStart":true});
            fillet(context, id + "F11", {"entities" : qUnion([Q0, Q1, Q2, Q3, Q4, Q5, Q6, Q7]), "radius" : 1.5 * mm, "tangentPropagation" : true, "allowEdgeOverflow" : false});
        }
    });
